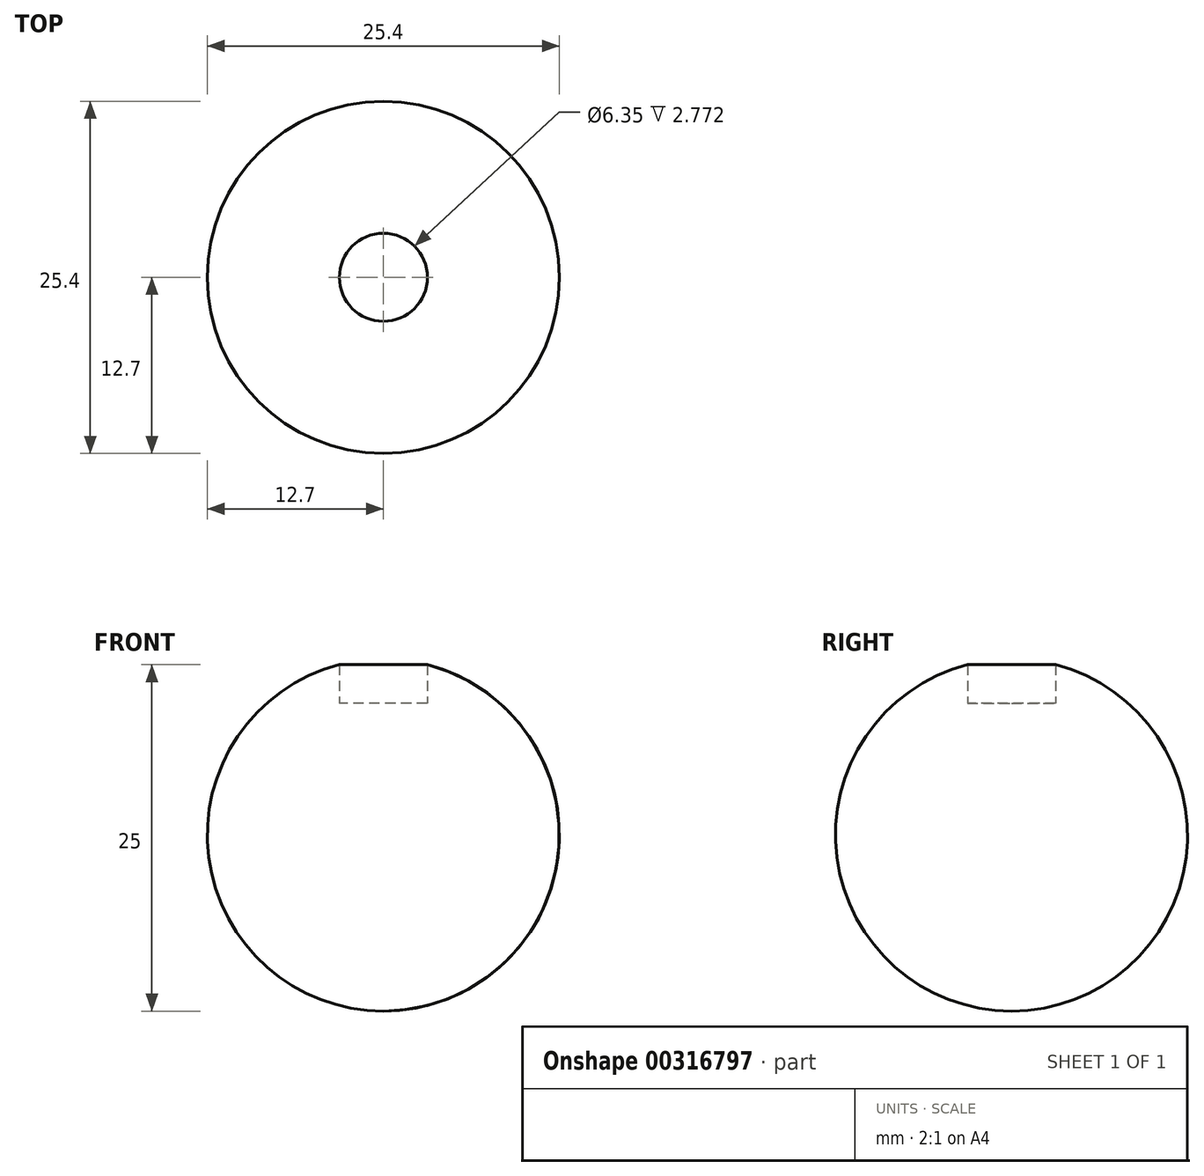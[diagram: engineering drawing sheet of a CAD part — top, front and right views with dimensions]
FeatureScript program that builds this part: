
annotation { "Feature Type Name" : "Feature", "Feature Type Description" : "" }
export const myFeature = defineFeature(function(context is Context, id is Id, definition is map)
    precondition{}
    {
        {
            var Q0;
            Q0=qCreatedBy(makeId("Front.planeOp"),FACE);
            var sketch = newSketch(context, id + "F0", { "sketchPlane" : qUnion([Q0])});
            skArc(sketch, "E0", {"start": v(0, 12.7) * mm, "mid": v(-12.7, 0) * mm, "end": v(0, -12.7) * mm});
            skLineSegment(sketch, "E1", {"start": v(0, 12.7) * mm, "end": v(0, -12.7) * mm});
            skSolve(sketch);
        }
        {
            var Q0;
            Q0=qCreatedBy(makeId("Top.planeOp"),FACE);
            var sketch = newSketch(context, id + "F1", { "sketchPlane" : qUnion([Q0])});
            skCircle(sketch, "E2", {"center": v(0, 0) * mm, "radius": 12.7 * mm});
            skSolve(sketch);
        }
        {
            var Q0;
            Q0=makeQuery(id+"F0.imprint","IMPRINT",FACE,{"disambiguationData":[TD([[makeQuery(id+"F0.imprint","IMPRINT",EDGE,{"derivedFrom":sQuery(id+"F0.wireOp",EDGE,"E0")}),1.0]])]});
            var Q1;
            Q1=sQuery(id+"F1.wireOp",EDGE,"E2");
            revolve(context, id + "F2", {"entities" : qUnion([Q0]), "axis" : qUnion([Q1]), "revolveType" : RevolveType.FULL});
        }
        {
            var Q0;
            Q0=qCreatedBy(makeId("Top.planeOp"),FACE);
            cPlane(context, id + "F3", {"entities" : qUnion([Q0]), "cplaneType" : CPlaneType.OFFSET, "offset" : 9.52 * mm, "width" : 152.4 * mm, "height" : 152.4 * mm});
        }
        {
            var Q0;
            Q0=qCreatedBy(id+"F3.planeOp",FACE);
            var sketch = newSketch(context, id + "F4", { "sketchPlane" : qUnion([Q0])});
            skCircle(sketch, "E3", {"center": v(0, 0) * mm, "radius": 3.18 * mm});
            skSolve(sketch);
        }
        {
            var Q0;
            Q0=makeQuery(id+"F4.imprint","IMPRINT",FACE,{"disambiguationData":[TD([[makeQuery(id+"F4.imprint","IMPRINT",EDGE,{"derivedFrom":sQuery(id+"F4.wireOp",EDGE,"E3")}),1.0]])]});
            var Q1;
            Q1=sQuery(id+"F4.wireOp",EDGE,"E3");
            extrude(context, id + "F5", {"entities" : qUnion([Q0]), "surfaceEntities" : qUnion([Q1]), "depth" : 25.4 * mm});
        }
        {
            var Q0;
            Q0=makeQuery(id+"F5.opExtrude","SWEPT_BODY",BODY,{"disambiguationData":[OSD([sQuery(id+"F4.wireOp",EDGE,"E3")])]});
            var Q1;
            Q1=makeQuery(id+"F2.opRevolve","SWEPT_BODY",BODY,{"disambiguationData":[OSD([sQuery(id+"F0.wireOp",EDGE,"E0"),sQuery(id+"F0.wireOp",EDGE,"E1")])]});
            booleanBodies(context, id + "F6", {"operationType" : BooleanOperationType.SUBTRACTION, "tools" : qUnion([Q0]), "targets" : qUnion([Q1])});
        }
    });
